# Revit family: 15-SANITARIO MONTECARLO NOVO HET AL BLCO
name_source: partatom
category: Aparatos sanitarios
revit_build: Autodesk Revit 2018 (Build: 20170223_1515(x64)
units: mm (PartAtom-declared; Revit-internal decimal feet)

## family parameters
Anfitrión = Muro
Compartido = No
Corte con vacíos al cargar = No
Cota de conector redondo = Diámetro de uso
Número OmniClass = 23.45.55.00
Punto de cálculo de habitación = No
Siempre vertical = Sí
Tipo de pieza = Normal
Título OmniClass = Sanitary Faucets, Wastes

## types (1)
- Tipo 1
    Acabado = Brillante
    Alto Nominal = 435 mm  [stored 1.42717 ft]
    Ancho Nominal = 635 mm
    Característica = Asiento de cierre suave para mayor comodidad, sifón esmaltado para optimizar el funcionamiento y limpieza del sanitario, diseño orgánico y contemporaneo
    Color = Blanco
    Consumo de Agua = Consumo de agua de 6,0 - 4,0 Lpf. (1,6 - 1,0 Gpf ) por descarga
    Cumplimiento de Norma = Ahorro de agua (4,0 - 6,0 litros por descarga)
    Código de montaje = D2030
    Descripción = Sanitario Manantial dos piezas descarga sencilla con botón superior
    Descripción IFC = Montecarlo novo het sanitario de una pieza
    Descripción de la garantía = Porcelana sanitaria garantía para siempre, garantía de 5 años para grifería tanque y asiento
    Diámetro de conexión de entrada = 12,7 mm / 1/2"
    Diámetro de conexión sanitaria = 101.6 mm / 4"
    Duración Garantía Partes = Completa para siempre
    Duración Garantía Unidad = Años
    Fabricante = www.corona.com.co
    Forma = Rectangular
    Imagen de tipo = <Ninguno>
    Informacion del producto = https://corona.co
    Longitud Nominal = 750 mm  [stored 2.46063 ft]
    Material = Ceramica_Corona_Blanco
    Material Secundario = Plastico_Corona_Blanco
    Nombre = Sanitario Montecarlo
    Nombre del Fabricante = Corona
    Numero de Modelo = O29161001
    Presión máxima = 80 PSI
    Presión mínima = 20 PSI
    Requerimientos de Accesibilidad = Manual
    Responsable Garantia Partes = www.corona.com.co
    Tamaño = 750 x 435 x 635
    Tipo de Activo = Fijo
    Tráfico = Residencial

note: [stored X ft] marks values corroborated as IEEE doubles in the binary element streams (Revit-internal decimal feet)
